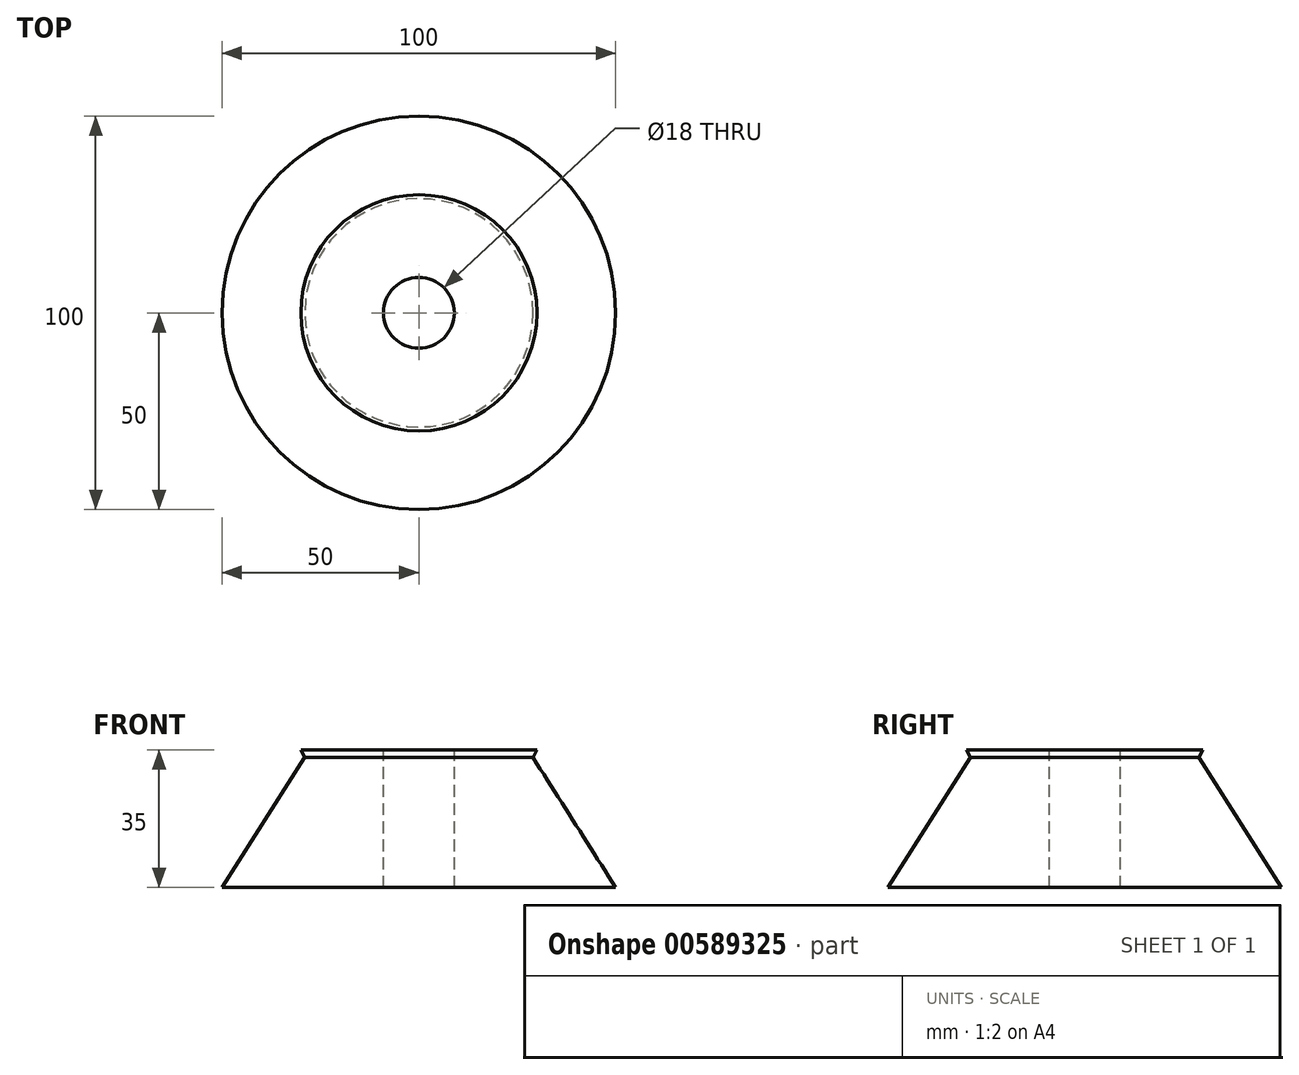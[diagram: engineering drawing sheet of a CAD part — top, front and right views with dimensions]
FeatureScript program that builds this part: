
annotation { "Feature Type Name" : "Feature", "Feature Type Description" : "" }
export const myFeature = defineFeature(function(context is Context, id is Id, definition is map)
    precondition{}
    {
        {
            var Q0;
            Q0=qCreatedBy(makeId("Front.planeOp"),FACE);
            var sketch = newSketch(context, id + "F0", { "sketchPlane" : qUnion([Q0])});
            skLineSegment(sketch, "E0", {"start": v(0, 0) * mm, "end": v(0, -35) * mm});
            skLineSegment(sketch, "E1", {"start": v(0, 0) * mm, "end": v(-30, 0) * mm});
            skLineSegment(sketch, "E2", {"start": v(-30, 0) * mm, "end": v(-29, -2) * mm});
            skLineSegment(sketch, "E3", {"start": v(-29, -2) * mm, "end": v(-50, -35) * mm});
            skLineSegment(sketch, "E4", {"start": v(-50, -35) * mm, "end": v(0, -35) * mm});
            skSolve(sketch);
        }
        {
            var Q0;
            Q0=makeQuery(id+"F0.imprint","IMPRINT",FACE,{"disambiguationData":[TD([[makeQuery(id+"F0.imprint","IMPRINT",EDGE,{"derivedFrom":sQuery(id+"F0.wireOp",EDGE,"E0")}),-1.0]])]});
            var Q1;
            Q1=sQuery(id+"F0.wireOp",EDGE,"E0");
            revolve(context, id + "F1", {"entities" : qUnion([Q0]), "axis" : qUnion([Q1]), "revolveType" : RevolveType.FULL});
        }
        {
            var Q0;
            Q0=makeQuery(id+"F1.opRevolve","SWEPT_FACE",FACE,{"disambiguationData":[OSD([sQuery(id+"F0.wireOp",EDGE,"E1")])]});
            var sketch = newSketch(context, id + "F2", { "sketchPlane" : qUnion([Q0])});
            skCircle(sketch, "E5", {"center": v(0, 0) * mm, "radius": 9 * mm});
            skSolve(sketch);
        }
        {
            var Q0;
            Q0=makeQuery(id+"F2.imprint","IMPRINT",FACE,{"disambiguationData":[TD([[makeQuery(id+"F2.imprint","IMPRINT",EDGE,{"derivedFrom":sQuery(id+"F2.wireOp",EDGE,"E5")}),1.0]])]});
            extrude(context, id + "F3", {"entities" : qUnion([Q0]), "operationType" : NewBodyOperationType.REMOVE, "endBound" : BoundingType.THROUGH_ALL, "oppositeDirection" : true, "depth" : 25.4 * mm, "offsetDistance" : 25.4 * mm});
        }
    });
